# Revit family: Condensate_Pump-Multi_Purpose-Zoeller-(521-0006)
name_source: partatom
category: Mechanical Equipment
revit_build: Autodesk Revit 2014 (Build: 20130308_1515(x64)
units: mm (PartAtom-declared; Revit-internal decimal feet)

## types (1)
- 521-0006
    Assembly Code = D3090200
    Capacity = 1 gallon (4 liter)
    Cord Length = 72"
    Cord Type = Grounded Plug
    Default Elevation = 0"
    Description = Multi-Purpose Condensate Pump
    Discharge Diameter = 3/8"
    Height = 4 1/4"
    Hertz = 60
    Horse Power = 1/6
    Inlet Diameter Connection = 1 1/8"
    Length = 11 1/2"
    Manufacturer = Zoeller
    Material = Plastic-Zoeller-Black
    Max. Flow Rate = 102 GPH (386 LPM)
    Max. Head = 20 ft. (6 m)
    Max. Operating Temp. = 140 °F
    Model = 521-0006
    Phase = 1
    Price = Prices may vary. Please consult Manufacturer Representative for most up-to-date price list.
    Product Documentation Link = http://cdn.qleapahead.com
    Product Page URL = http://www.zoellerpumps.com
    URL = http://www.zoellerpumps.com
    Voltage = 115 V
    Width = 5 1/4"

## geometry (parser evidence)
native form markers: Sweep x3
no freeform markers — native parametric forms only
